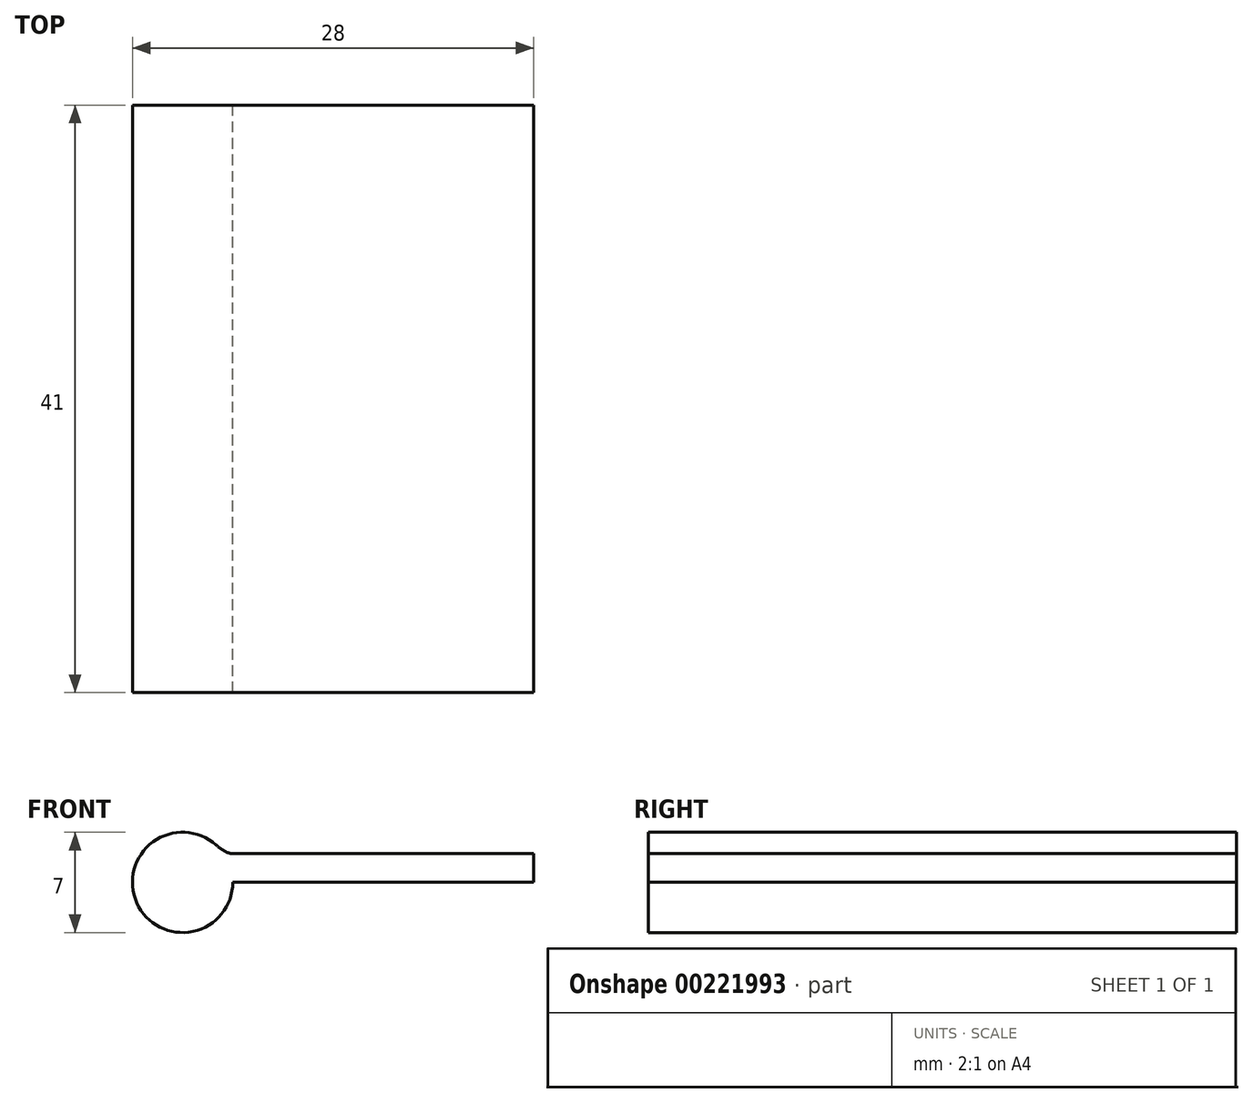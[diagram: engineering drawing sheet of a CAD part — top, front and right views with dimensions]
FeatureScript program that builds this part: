
annotation { "Feature Type Name" : "Feature", "Feature Type Description" : "" }
export const myFeature = defineFeature(function(context is Context, id is Id, definition is map)
    precondition{}
    {
        {
            var Q0;
            Q0=qCreatedBy(makeId("Front.planeOp"),FACE);
            var sketch = newSketch(context, id + "F0", { "sketchPlane" : qUnion([Q0])});
            skLineSegment(sketch, "E0.bottom", {"start": v(10.5, -1) * mm, "end": v(-10.5, -1) * mm});
            skLineSegment(sketch, "E0.top", {"start": v(10.5, 1) * mm, "end": v(-10.5, 1) * mm});
            skLineSegment(sketch, "E0.left", {"start": v(10.5, -1) * mm, "end": v(10.5, 1) * mm});
            skLineSegment(sketch, "E0.right", {"start": v(-10.5, -1) * mm, "end": v(-10.5, 1) * mm});
            skPoint(sketch, "E0.middle", {"position": v(0, 0) * mm});
            skCircle(sketch, "E1", {"center": v(-14, -1) * mm, "radius": 3.5 * mm});
            skLineSegment(sketch, "E2", {"start": v(-10.5, -1) * mm, "end": v(-14, -1) * mm});
            skFitSpline(sketch, "E3", {"points": [v(-10.5, 1) * mm, v(-11.67, 1.6) * mm], "startDerivative": vector(-1.2, 0) * mm, "endDerivative": vector(-0.9, 0.8) * mm});
            skSolve(sketch);
        }
        {
            var Q0;
            Q0 = qSketchRegion(id + "F0", true);
            extrude(context, id + "F1", {"entities" : qUnion([Q0]), "endBound" : BoundingType.SYMMETRIC, "depth" : 41 * mm});
        }
    });
